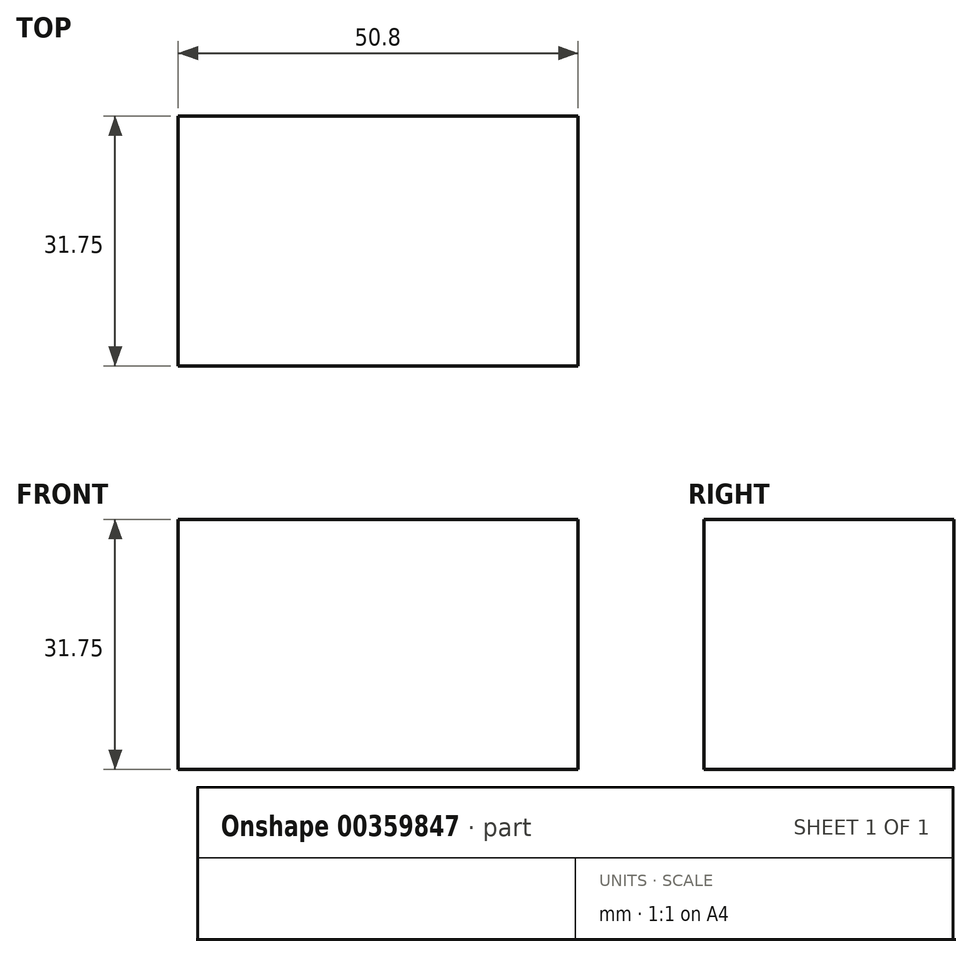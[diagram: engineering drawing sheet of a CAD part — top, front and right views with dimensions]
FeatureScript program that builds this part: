
annotation { "Feature Type Name" : "Feature", "Feature Type Description" : "" }
export const myFeature = defineFeature(function(context is Context, id is Id, definition is map)
    precondition{}
    {
        {
            var Q0;
            Q0=qCreatedBy(makeId("Front.planeOp"),FACE);
            var sketch = newSketch(context, id + "F0", { "sketchPlane" : qUnion([Q0])});
            skLineSegment(sketch, "E0", {"start": v(0, 0) * mm, "end": v(50.8, 0) * mm});
            skLineSegment(sketch, "E1", {"start": v(50.8, 0) * mm, "end": v(50.8, 31.75) * mm});
            skLineSegment(sketch, "E2", {"start": v(50.8, 31.75) * mm, "end": v(0, 31.75) * mm});
            skLineSegment(sketch, "E3", {"start": v(0, 31.75) * mm, "end": v(0, 0) * mm});
            skSolve(sketch);
        }
        {
            var Q0;
            Q0=makeQuery(id+"F0.imprint","IMPRINT",FACE,{"disambiguationData":[TD([[makeQuery(id+"F0.imprint","IMPRINT",EDGE,{"derivedFrom":sQuery(id+"F0.wireOp",EDGE,"E0")}),1.0]])]});
            extrude(context, id + "F1", {"entities" : qUnion([Q0]), "depth" : 31.75 * mm});
        }
    });
